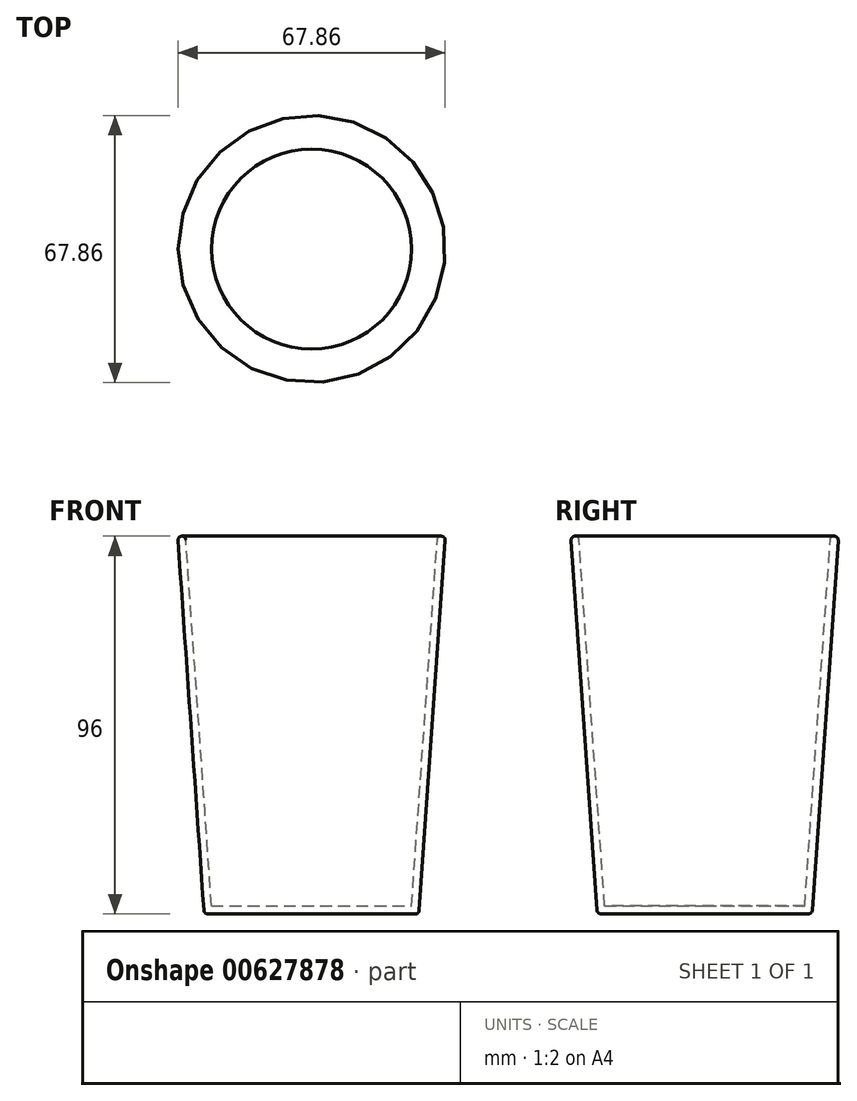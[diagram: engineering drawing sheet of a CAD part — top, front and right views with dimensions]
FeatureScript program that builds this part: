
annotation { "Feature Type Name" : "Feature", "Feature Type Description" : "" }
export const myFeature = defineFeature(function(context is Context, id is Id, definition is map)
    precondition{}
    {
        {
            var Q0;
            Q0=qCreatedBy(makeId("Front.planeOp"),FACE);
            var sketch = newSketch(context, id + "F0", { "sketchPlane" : qUnion([Q0])});
            skLineSegment(sketch, "E0", {"start": v(-34, 79.55) * mm, "end": v(-27.29, -16.45) * mm});
            skLineSegment(sketch, "E1", {"start": v(-27.29, -16.45) * mm, "end": v(0, -16.45) * mm});
            skLineSegment(sketch, "E2", {"start": v(0, -16.45) * mm, "end": v(0, -14.45) * mm});
            skLineSegment(sketch, "E3", {"start": v(0, -14.45) * mm, "end": v(-25.42, -14.45) * mm});
            skLineSegment(sketch, "E4", {"start": v(-25.42, -14.45) * mm, "end": v(-32, 79.55) * mm});
            skLineSegment(sketch, "E5", {"start": v(-32, 79.55) * mm, "end": v(-34, 79.55) * mm});
            skSolve(sketch);
        }
        {
            var Q0;
            Q0 = qSketchRegion(id + "F0", true);
            var Q1;
            Q1=sQuery(id+"F0.wireOp",EDGE,"E2");
            revolve(context, id + "F1", {"entities" : qUnion([Q0]), "axis" : qUnion([Q1]), "revolveType" : RevolveType.FULL});
        }
        {
            var Q0;
            Q0=makeQuery(id+"F1.opRevolve","SWEPT_EDGE",EDGE,{"disambiguationData":[OSD([sQuery(id+"F0.wireOp",EDGE,"E0"),sQuery(id+"F0.wireOp",EDGE,"E1")])]});
            var Q1;
            Q1=makeQuery(id+"F1.opRevolve","SWEPT_EDGE",EDGE,{"disambiguationData":[OSD([sQuery(id+"F0.wireOp",EDGE,"E0"),sQuery(id+"F0.wireOp",EDGE,"E5")])]});
            var Q2;
            Q2=makeQuery(id+"F1.opRevolve","SWEPT_EDGE",EDGE,{"disambiguationData":[OSD([sQuery(id+"F0.wireOp",EDGE,"E4"),sQuery(id+"F0.wireOp",EDGE,"E5")])]});
            fillet(context, id + "F2", {"entities" : qUnion([Q0, Q1, Q2]), "radius" : 1 * mm, "tangentPropagation" : true, "allowEdgeOverflow" : false});
        }
    });
